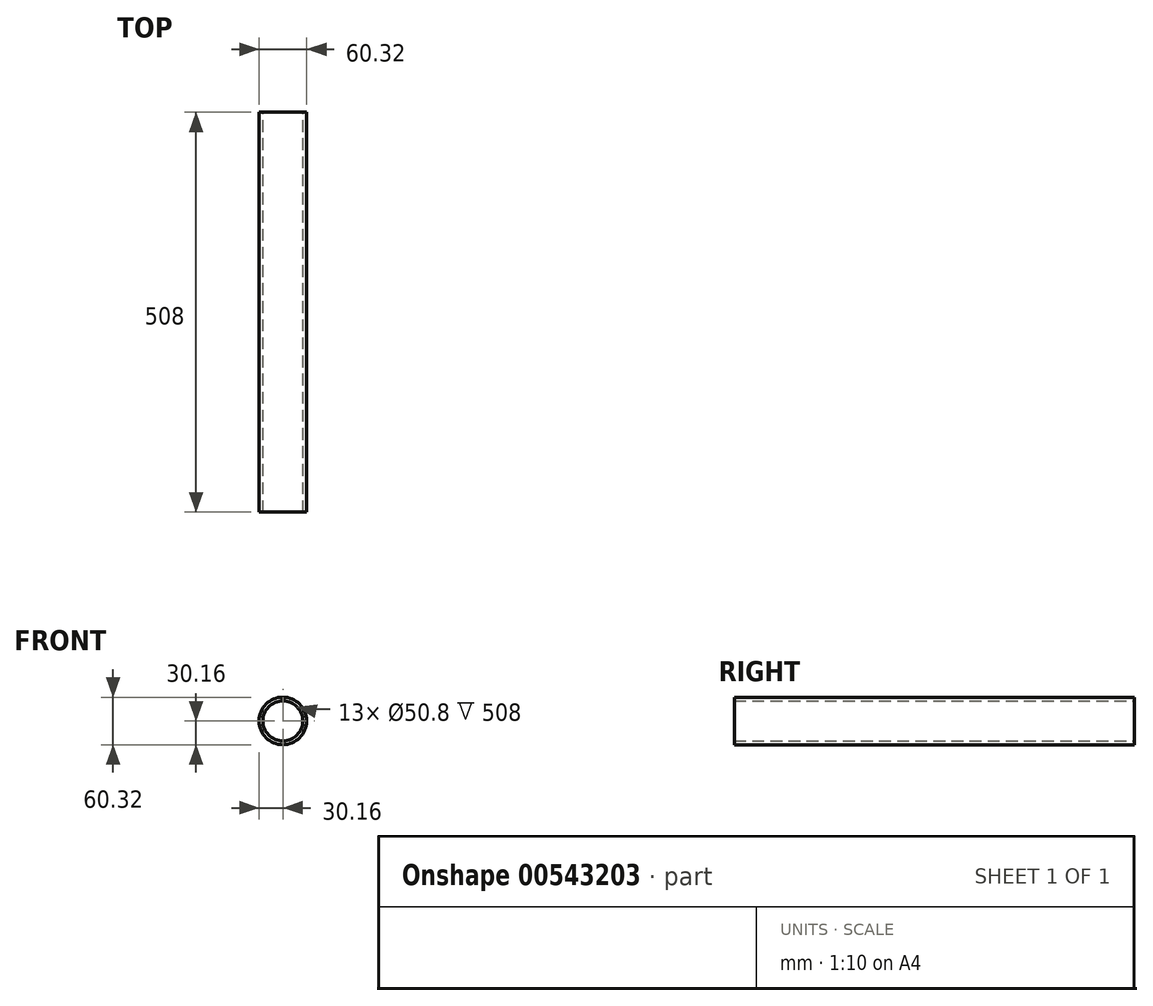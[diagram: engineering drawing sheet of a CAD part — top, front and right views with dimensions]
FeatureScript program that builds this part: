
annotation { "Feature Type Name" : "Feature", "Feature Type Description" : "" }
export const myFeature = defineFeature(function(context is Context, id is Id, definition is map)
    precondition{}
    {
        {
            var Q0;
            Q0=qCreatedBy(makeId("Front.planeOp"),FACE);
            var sketch = newSketch(context, id + "F0", { "sketchPlane" : qUnion([Q0])});
            skCircle(sketch, "E0", {"center": v(0, 0) * mm, "radius": 30.16 * mm});
            skCircle(sketch, "E1", {"center": v(0, 0) * mm, "radius": 25.4 * mm});
            skSolve(sketch);
        }
        {
            var Q0;
            Q0=qSketchRegion(id+"F0",true);
            extrude(context, id + "F1", {"entities" : qUnion([Q0]), "depth" : 508 * mm, "offsetDistance" : 25.4 * mm, "symmetric" : true});
        }
    });
